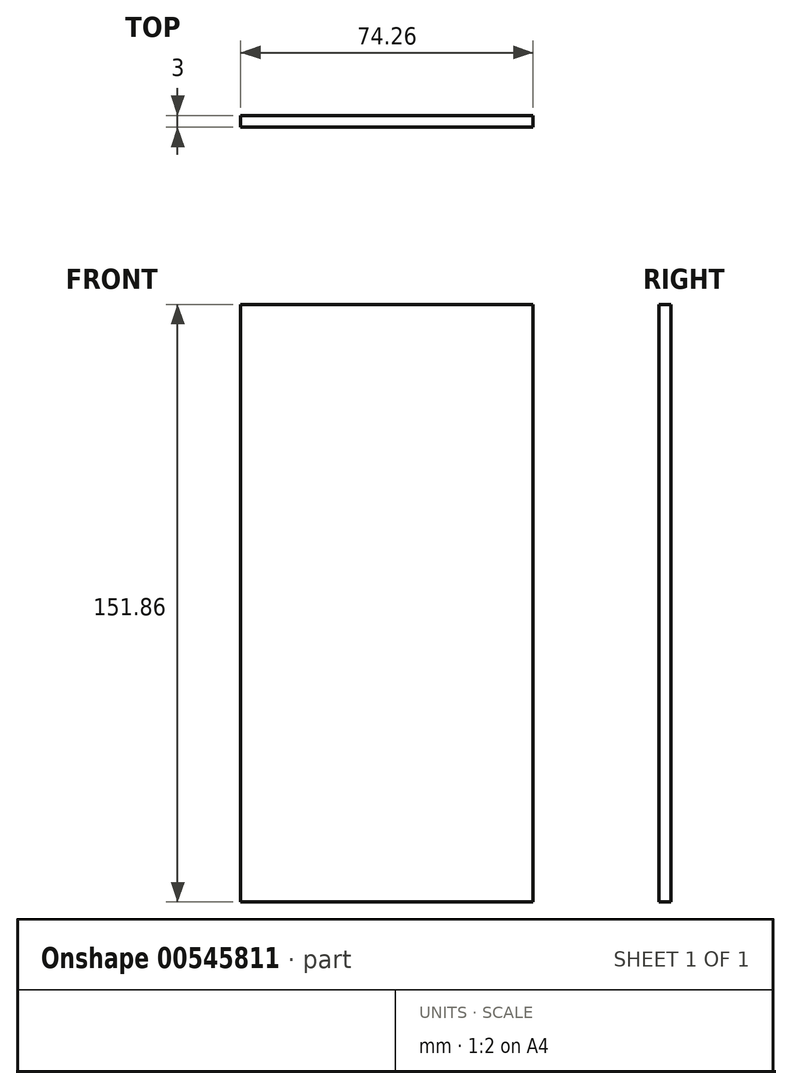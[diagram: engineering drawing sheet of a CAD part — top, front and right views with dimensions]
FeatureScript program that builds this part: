
annotation { "Feature Type Name" : "Feature", "Feature Type Description" : "" }
export const myFeature = defineFeature(function(context is Context, id is Id, definition is map)
    precondition{}
    {
        {
            var Q0;
            Q0=qCreatedBy(makeId("Front.planeOp"),FACE);
            var sketch = newSketch(context, id + "F0", { "sketchPlane" : qUnion([Q0])});
            skLineSegment(sketch, "E0.bottom", {"start": v(37.13, -75.93) * mm, "end": v(-37.13, -75.93) * mm});
            skLineSegment(sketch, "E0.top", {"start": v(37.13, 75.93) * mm, "end": v(-37.13, 75.93) * mm});
            skLineSegment(sketch, "E0.left", {"start": v(37.13, -75.93) * mm, "end": v(37.13, 75.93) * mm});
            skLineSegment(sketch, "E0.right", {"start": v(-37.13, -75.93) * mm, "end": v(-37.13, 75.93) * mm});
            skPoint(sketch, "E0.middle", {"position": v(0, 0) * mm});
            skSolve(sketch);
        }
        {
            var Q0;
            Q0=makeQuery(id+"F0.imprint","IMPRINT",FACE,{"disambiguationData":[TD([[makeQuery(id+"F0.imprint","IMPRINT",EDGE,{"derivedFrom":sQuery(id+"F0.wireOp",EDGE,"E0.bottom")}),-1.0]])]});
            extrude(context, id + "F1", {"entities" : qUnion([Q0]), "depth" : 3 * mm, "offsetDistance" : 25.4 * mm});
        }
    });
